# Revit family: SHR1200-SER1100
name_source: partatom
category: Mechanical Equipment
revit_build: Autodesk Revit 2016 (Build: 20170117_1200(x64)
units: mm (PartAtom-declared; Revit-internal decimal feet)

## family parameters
Always vertical = Yes
Cut with Voids When Loaded = No
OmniClass Number = 23.75.00.00
OmniClass Title = Climate Control (HVAC)
Part Type = Normal
Room Calculation Point = No
Round Connector Dimension = Use Diameter
Shared = No
Work Plane-Based = No

## types (3) — shared parameters
Apparent Load = 1400 W
Current = 11.67 A
Load Classification = HVAC
Manufacturer = Fantech
Number of poles = 1
Power Factor = 1
Voltage = 120 V
Width = 506.9 mm

## per-type parameters (varying)
| type | Average Airflow | BPM | Description | Model | Product number | URL | Weight | construction | not bpm |
| SER 1100 | 1179 CFM | No | Light Commercial Energy Recovery Ventilators | SER 1100 | 99277 | http://www.fantech.net ec-vent/ | 210 lbs | 0 | Yes |
| SHR 1200 | 1219 CFM | No | Commercial Heat Recovery Ventilators | SHR 1200 | 99272 | http://www.fantech.net | 240 lbs | 0 | Yes |
| SHR 1200 BPM | 1219 CFM | Yes | Commercial Heat Recovery Ventilators | SHR 1200 | 99272, 99301 | http://www.fantech.net | 240 lbs | 99 | No |

## geometry (parser evidence)
native form markers: Blend x2, Sweep x3
no freeform markers — native parametric forms only
